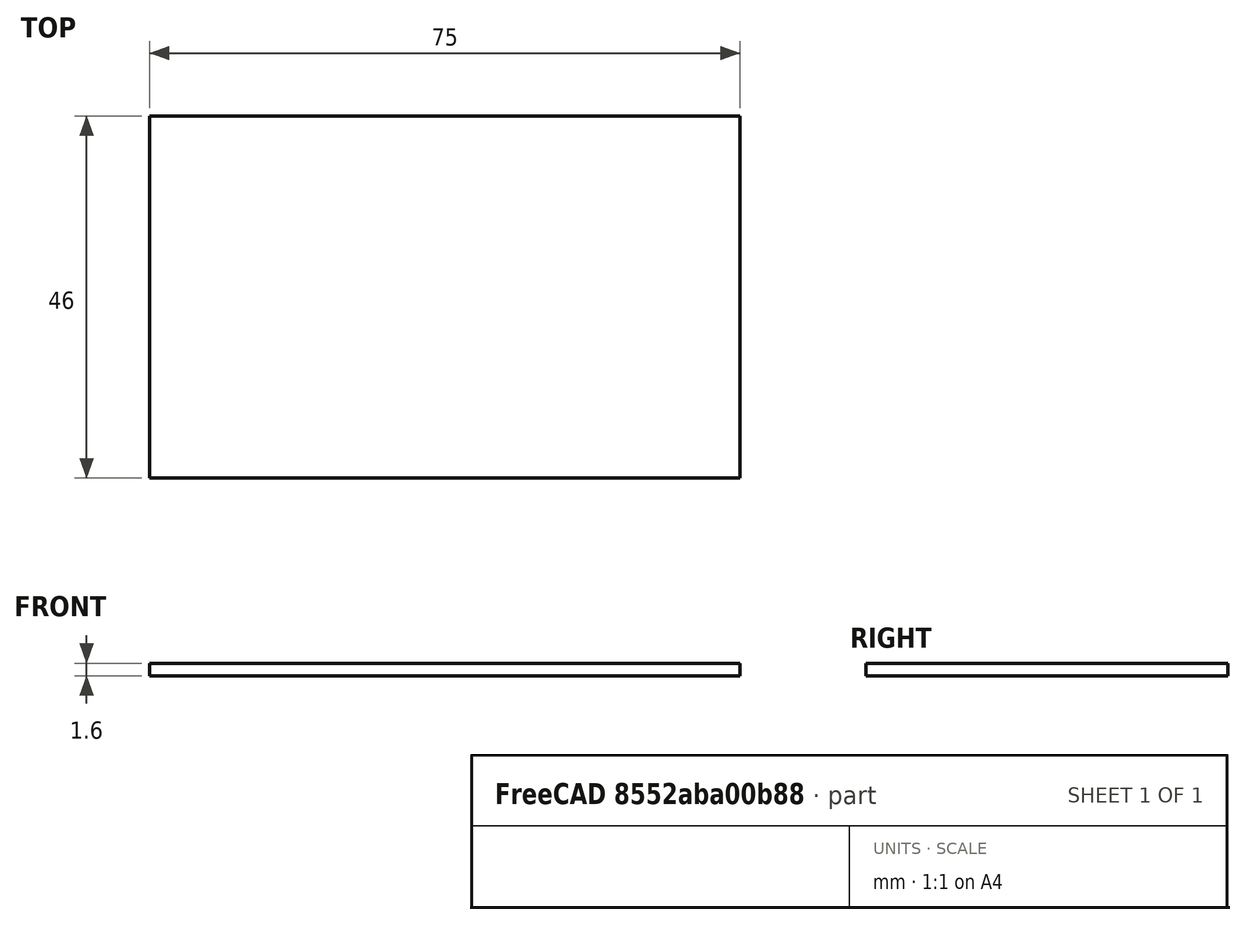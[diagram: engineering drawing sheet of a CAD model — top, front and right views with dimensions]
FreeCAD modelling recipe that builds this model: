
FCSTD DOCUMENT  (FreeCAD 0.19R24267 +148 (Git))
Label: LiulinPcbPlate
License: All rights reserved
LicenseURL: http://en.wikipedia.org/wiki/All_rights_reserved
objects: Sketcher::SketchObject×1, PartDesign::Pad×1, PartDesign::Body×1
note: 4 computed .brp shape members not serialized (recipe doc carries the construction recipe); baked Part::Feature solids carry a one-line shape summary decoded from their .brp

FEATURE [Sketcher::SketchObject] Sketch
  FullyConstrained = true
  MapMode = 5
  Support = -> [XY_Plane]
  sketch-geometry (4):
    g0: LineSegment StartX=-37.5 StartY=23 StartZ=0 EndX=37.5 EndY=23 EndZ=0
    g1: LineSegment StartX=37.5 StartY=23 StartZ=0 EndX=37.5 EndY=-23 EndZ=0
    g2: LineSegment StartX=37.5 StartY=-23 StartZ=0 EndX=-37.5 EndY=-23 EndZ=0
    g3: LineSegment StartX=-37.5 StartY=-23 StartZ=0 EndX=-37.5 EndY=23 EndZ=0
  constraints (11):
    c: Coincident(g0,g1)
    c: Coincident(g1,g2)
    c: Coincident(g2,g3)
    c: Coincident(g3,g0)
    c: Horizontal(g0)
    c: Horizontal(g2)
    c: Vertical(g1)
    c: Vertical(g3)
    c: DistanceY(g1,g0) = 46
    c: DistanceX(g0,g0) = 75
    c: Symmetric(g0,g1,g-1)
FEATURE [PartDesign::Pad] Pad
  Direction = (1,1,1)
  Length = 1.6
  Length2 = 100
  Profile = -> Sketch
  Type = 0
FEATURE [PartDesign::Body] Body
  Group = -> [Sketch,Pad]
  Origin = -> Origin
  Tip = -> Pad
